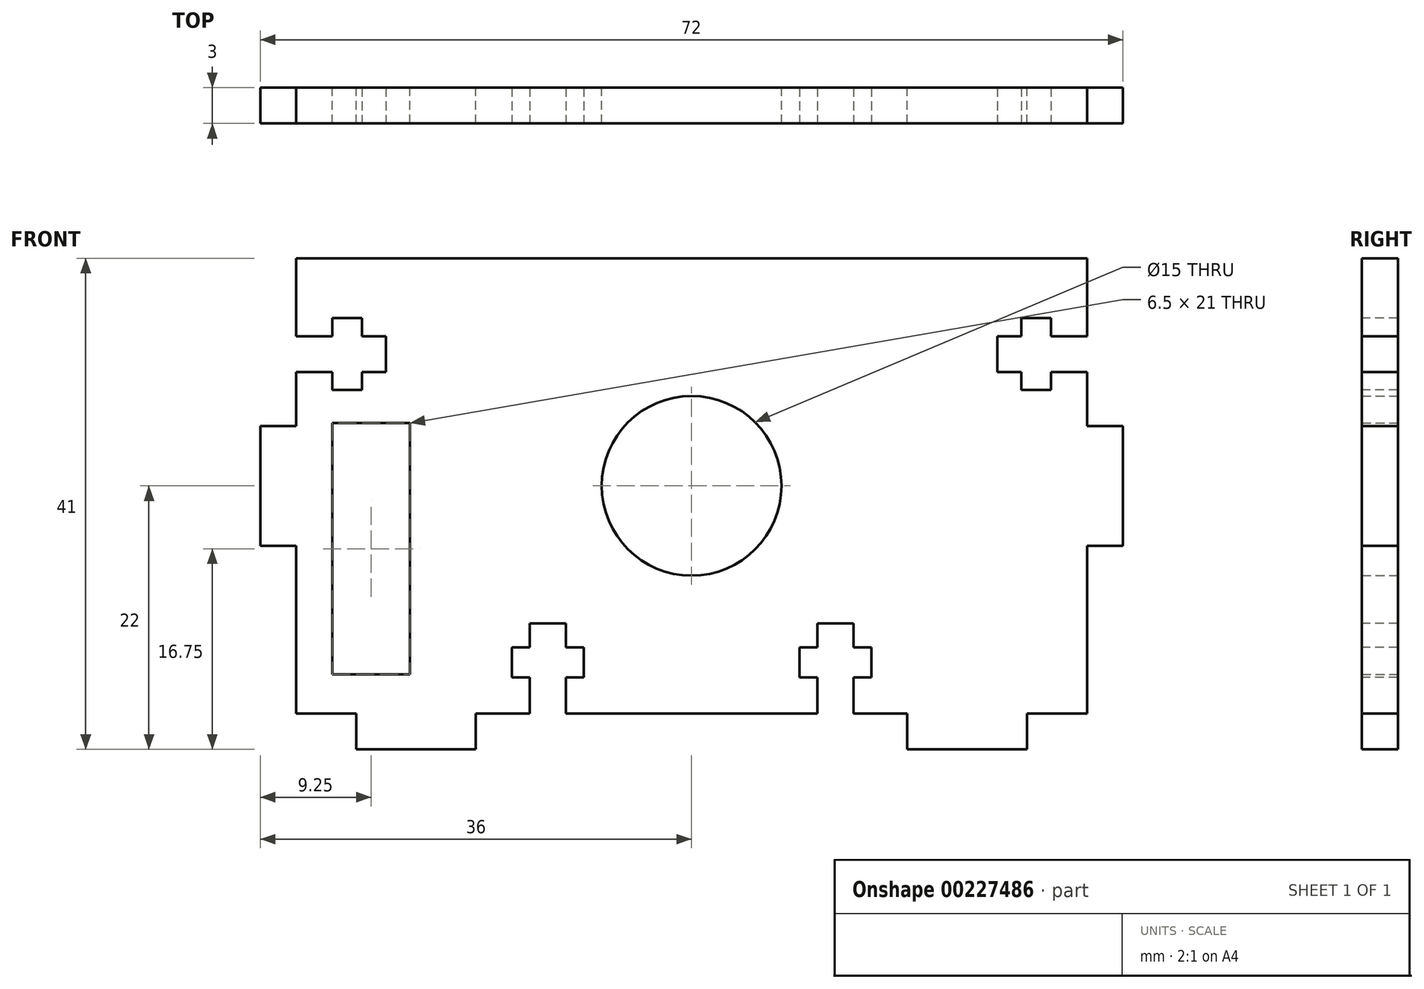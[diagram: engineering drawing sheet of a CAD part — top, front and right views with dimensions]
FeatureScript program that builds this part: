
annotation { "Feature Type Name" : "Feature", "Feature Type Description" : "" }
export const myFeature = defineFeature(function(context is Context, id is Id, definition is map)
    precondition{}
    {
        {
            assignVariable(context, id + "F0", {"name" : "Thickness", "anyValue" : 3});
        }
        {
            var Q0;
            Q0=qCreatedBy(makeId("Front.planeOp"),FACE);
            var sketch = newSketch(context, id + "F1", { "sketchPlane" : qUnion([Q0])});
            skLineSegment(sketch, "E0.top", {"start": v(33, 19) * mm, "end": v(-33, 19) * mm});
            skPoint(sketch, "E0.middle", {"position": v(0, 0) * mm});
            skCircle(sketch, "E1", {"center": v(0, 0) * mm, "radius": 7.5 * mm});
            skPoint(sketch, "E2", {"position": v(0, 19) * mm});
            skLineSegment(sketch, "E3", {"start": v(-28, -19) * mm, "end": v(-28, -22) * mm});
            skLineSegment(sketch, "E4", {"start": v(-28, -22) * mm, "end": v(-18, -22) * mm});
            skLineSegment(sketch, "E5", {"start": v(-18, -22) * mm, "end": v(-18, -19) * mm});
            skLineSegment(sketch, "E6", {"start": v(-18, -19) * mm, "end": v(0, -19) * mm});
            skLineSegment(sketch, "E7.MirrorCS", {"start": v(18, -19) * mm, "end": v(0, -19) * mm});
            skLineSegment(sketch, "E8.MirrorCS", {"start": v(18, -22) * mm, "end": v(18, -19) * mm});
            skLineSegment(sketch, "E9.MirrorCS", {"start": v(28, -22) * mm, "end": v(18, -22) * mm});
            skLineSegment(sketch, "E10.MirrorCS", {"start": v(28, -19) * mm, "end": v(28, -22) * mm});
            skLineSegment(sketch, "E11", {"start": v(-33, -19) * mm, "end": v(-33, -5) * mm});
            skLineSegment(sketch, "E12", {"start": v(-33, -5) * mm, "end": v(-36, -5) * mm});
            skLineSegment(sketch, "E13", {"start": v(-36, -5) * mm, "end": v(-36, 5) * mm});
            skLineSegment(sketch, "E14", {"start": v(-36, 5) * mm, "end": v(-33, 5) * mm});
            skLineSegment(sketch, "E15", {"start": v(-33, 5) * mm, "end": v(-33, 19) * mm});
            skPoint(sketch, "E16", {"position": v(-36, 0) * mm});
            skLineSegment(sketch, "E17.MirrorCS", {"start": v(33, 5) * mm, "end": v(33, 19) * mm});
            skLineSegment(sketch, "E18.MirrorCS", {"start": v(36, 5) * mm, "end": v(33, 5) * mm});
            skLineSegment(sketch, "E19.MirrorCS", {"start": v(36, -5) * mm, "end": v(36, 5) * mm});
            skLineSegment(sketch, "E20.MirrorCS", {"start": v(33, -5) * mm, "end": v(36, -5) * mm});
            skLineSegment(sketch, "E21.MirrorCS", {"start": v(33, -19) * mm, "end": v(33, -5) * mm});
            skLineSegment(sketch, "E22", {"start": v(28, -19) * mm, "end": v(33, -19) * mm});
            skLineSegment(sketch, "E23", {"start": v(-28, -19) * mm, "end": v(-33, -19) * mm});
            skLineSegment(sketch, "E24.bottom", {"start": v(-30, 5.25) * mm, "end": v(-23.5, 5.25) * mm});
            skLineSegment(sketch, "E24.top", {"start": v(-30, -15.75) * mm, "end": v(-23.5, -15.75) * mm});
            skLineSegment(sketch, "E24.left", {"start": v(-30, 5.25) * mm, "end": v(-30, -15.75) * mm});
            skLineSegment(sketch, "E24.right", {"start": v(-23.5, 5.25) * mm, "end": v(-23.5, -15.75) * mm});
            skSolve(sketch);
        }
        {
            var Q0;
            Q0=makeQuery(id+"F1.imprint","IMPRINT",FACE,{"disambiguationData":[TD([[makeQuery(id+"F1.imprint","IMPRINT",EDGE,{"derivedFrom":sQuery(id+"F1.wireOp",EDGE,"E0.bottom")}),-1.0]])]});
            var Q1;
            Q1=makeQuery(id+"F1.imprint","IMPRINT",FACE,{"disambiguationData":[TD([[makeQuery(id+"F1.imprint","IMPRINT",EDGE,{"derivedFrom":sQuery(id+"F1.wireOp",EDGE,"E0.top")}),1.0]])]});
            extrude(context, id + "F2", {"entities" : qUnion([Q0, Q1]), "depth" : (getVariable(context, 'Thickness')) * mm});
        }
        {
            var Q0;
            Q0=makeQuery(id+"F2.opExtrude","CAP_FACE",FACE,{"disambiguationData":[OSD([sQuery(id+"F1.wireOp",EDGE,"E0.top"),sQuery(id+"F1.wireOp",EDGE,"E1"),sQuery(id+"F1.wireOp",EDGE,"i2BJ4We7-Z1tz-6YYD-7Gnh-UwGsJDHukj4o"),sQuery(id+"F1.wireOp",EDGE,"H5TLaSxA-TAvm-WxYI-6s5p-rbUKsHJPtpz8"),sQuery(id+"F1.wireOp",EDGE,"fE5sAuBm-J1N4-LUQK-MxoP-oJGd3h4EWBky"),sQuery(id+"F1.wireOp",EDGE,"UVkaeSOW-HMeC-MlRq-fWxO-58zO0Vm4gzLd"),sQuery(id+"F1.wireOp",EDGE,"4oAcHBtJ-SWL1-Us38-5a5N-tiTYXxMsnVxl"),sQuery(id+"F1.wireOp",EDGE,"MGHFterx-abw6-INuc-nvHV-QaNsLm6ah1ng"),sQuery(id+"F1.wireOp",EDGE,"DztduCwT-NtgE-rZnK-mSEW-EnSqVKOmk10X"),sQuery(id+"F1.wireOp",EDGE,"XImseshz-UxQT-ogDy-5Lvy-O5B2oz8zv5fS"),sQuery(id+"F1.wireOp",EDGE,"FHz1HeJZ-Y50a-yfiC-Rnzm-b0fU7RSFoIpM"),sQuery(id+"F1.wireOp",EDGE,"bBcTDBjg-FDSx-XcTB-SbE1-9syf6QqrHLmC"),sQuery(id+"F1.wireOp",EDGE,"1vXtDNT1-yAZY-NYDk-InIM-wFA5S2rVquaF"),sQuery(id+"F1.wireOp",EDGE,"rcTIoJpC-EadT-N3WT-61kg-b3dVzh2UPf16"),sQuery(id+"F1.wireOp",EDGE,"V9EOst0m-YofT-ZeQ4-KXmd-etc1AHxpQRv2"),sQuery(id+"F1.wireOp",EDGE,"E3"),sQuery(id+"F1.wireOp",EDGE,"E4"),sQuery(id+"F1.wireOp",EDGE,"E5"),sQuery(id+"F1.wireOp",EDGE,"E6"),sQuery(id+"F1.wireOp",EDGE,"E7.MirrorCS"),sQuery(id+"F1.wireOp",EDGE,"E8.MirrorCS"),sQuery(id+"F1.wireOp",EDGE,"E9.MirrorCS"),sQuery(id+"F1.wireOp",EDGE,"E10.MirrorCS"),sQuery(id+"F1.wireOp",EDGE,"4fc586d0-1a2d-4033-9ad1-b4b14924f1e60.MirrorCS"),sQuery(id+"F1.wireOp",EDGE,"25921314-2feb-4960-9358-c6f40c29e8060.MirrorCS"),sQuery(id+"F1.wireOp",EDGE,"92609e8c-4cca-44cb-b192-d1e8ea80d6400.MirrorCS"),sQuery(id+"F1.wireOp",EDGE,"c6435143-3ef5-4a16-a53c-0c7a1f294e250.MirrorCS"),sQuery(id+"F1.wireOp",EDGE,"302a1fd6-7f51-4dcd-b85b-b87c70c5ff6f0.MirrorCS"),sQuery(id+"F1.wireOp",EDGE,"271ff51f-9e70-48b1-9ca4-6ffa4ba6ee090.MirrorCS"),sQuery(id+"F1.wireOp",EDGE,"7c8ad784-0027-4aca-88da-cb9512f49f770.MirrorCS"),sQuery(id+"F1.wireOp",EDGE,"aab8c399-5e78-4643-9a76-05bc1427fb740.MirrorCS"),sQuery(id+"F1.wireOp",EDGE,"2a5f69ab-9c37-4cf4-a27a-83d52b59f34f0.MirrorCS"),sQuery(id+"F1.wireOp",EDGE,"8a72d888-9ff6-4074-9ea7-52382edc54d80.MirrorCS"),sQuery(id+"F1.wireOp",EDGE,"2b144515-558f-4b7e-bfd9-8a7150f656b50.MirrorCS"),sQuery(id+"F1.wireOp",EDGE,"7271def4-b984-4847-8607-e135956054630.MirrorCS"),sQuery(id+"F1.wireOp",EDGE,"d1406031-9f0b-476a-854e-e83de3dd73970.MirrorCS"),sQuery(id+"F1.wireOp",EDGE,"E11"),sQuery(id+"F1.wireOp",EDGE,"E12"),sQuery(id+"F1.wireOp",EDGE,"E13"),sQuery(id+"F1.wireOp",EDGE,"E14"),sQuery(id+"F1.wireOp",EDGE,"E15"),sQuery(id+"F1.wireOp",EDGE,"E17.MirrorCS"),sQuery(id+"F1.wireOp",EDGE,"E18.MirrorCS"),sQuery(id+"F1.wireOp",EDGE,"E19.MirrorCS"),sQuery(id+"F1.wireOp",EDGE,"E20.MirrorCS"),sQuery(id+"F1.wireOp",EDGE,"E21.MirrorCS")])],"isStart":false});
            var sketch = newSketch(context, id + "F3", { "sketchPlane" : qUnion([Q0])});
            skLineSegment(sketch, "E25", {"start": v(10.5, -19) * mm, "end": v(10.5, -16) * mm});
            skLineSegment(sketch, "E26", {"start": v(10.5, -16) * mm, "end": v(9, -16) * mm});
            skLineSegment(sketch, "E27", {"start": v(9, -16) * mm, "end": v(9, -13.5) * mm});
            skLineSegment(sketch, "E28", {"start": v(9, -13.5) * mm, "end": v(10.5, -13.5) * mm});
            skLineSegment(sketch, "E29", {"start": v(10.5, -13.5) * mm, "end": v(10.5, -11.5) * mm});
            skLineSegment(sketch, "E30", {"start": v(10.5, -11.5) * mm, "end": v(13.5, -11.5) * mm});
            skLineSegment(sketch, "E31", {"start": v(13.5, -11.5) * mm, "end": v(13.5, -13.5) * mm});
            skLineSegment(sketch, "E32", {"start": v(13.5, -13.5) * mm, "end": v(15, -13.5) * mm});
            skLineSegment(sketch, "E33", {"start": v(15, -13.5) * mm, "end": v(15, -16) * mm});
            skLineSegment(sketch, "E34", {"start": v(15, -16) * mm, "end": v(13.5, -16) * mm});
            skLineSegment(sketch, "E35", {"start": v(13.5, -16) * mm, "end": v(13.5, -19) * mm});
            skPoint(sketch, "E36", {"position": v(12, -19) * mm});
            skLineSegment(sketch, "E37", {"start": v(13.5, -19) * mm, "end": v(10.5, -19) * mm});
            skLineSegment(sketch, "E38", {"start": v(30, 9.5) * mm, "end": v(30, 8) * mm});
            skLineSegment(sketch, "E39", {"start": v(30, 8) * mm, "end": v(27.5, 8) * mm});
            skLineSegment(sketch, "E40", {"start": v(27.5, 8) * mm, "end": v(27.5, 9.5) * mm});
            skLineSegment(sketch, "E41", {"start": v(27.5, 9.5) * mm, "end": v(25.5, 9.5) * mm});
            skLineSegment(sketch, "E42", {"start": v(25.5, 9.5) * mm, "end": v(25.5, 12.5) * mm});
            skLineSegment(sketch, "E43", {"start": v(25.5, 12.5) * mm, "end": v(27.5, 12.5) * mm});
            skLineSegment(sketch, "E44", {"start": v(27.5, 12.5) * mm, "end": v(27.5, 14) * mm});
            skLineSegment(sketch, "E45", {"start": v(27.5, 14) * mm, "end": v(30, 14) * mm});
            skLineSegment(sketch, "E46", {"start": v(30, 14) * mm, "end": v(30, 12.5) * mm});
            skLineSegment(sketch, "E47", {"start": v(30, 12.5) * mm, "end": v(33, 12.5) * mm});
            skLineSegment(sketch, "E48.MirrorCS", {"start": v(-10.5, -16) * mm, "end": v(-9, -16) * mm});
            skLineSegment(sketch, "E49.MirrorCS", {"start": v(-9, -13.5) * mm, "end": v(-10.5, -13.5) * mm});
            skLineSegment(sketch, "E50.MirrorCS", {"start": v(-15, -16) * mm, "end": v(-13.5, -16) * mm});
            skLineSegment(sketch, "E51.MirrorCS", {"start": v(-13.5, -13.5) * mm, "end": v(-15, -13.5) * mm});
            skLineSegment(sketch, "E52.MirrorCS", {"start": v(-10.5, -13.5) * mm, "end": v(-10.5, -11.5) * mm});
            skLineSegment(sketch, "E53.MirrorCS", {"start": v(-13.5, -19) * mm, "end": v(-10.5, -19) * mm});
            skLineSegment(sketch, "E54.MirrorCS", {"start": v(-9, -16) * mm, "end": v(-9, -13.5) * mm});
            skPoint(sketch, "E55.MirrorP", {"position": v(-12, -19) * mm});
            skLineSegment(sketch, "E56.MirrorCS", {"start": v(-10.5, -19) * mm, "end": v(-10.5, -16) * mm});
            skLineSegment(sketch, "E57.MirrorCS", {"start": v(-10.5, -11.5) * mm, "end": v(-13.5, -11.5) * mm});
            skLineSegment(sketch, "E58.MirrorCS", {"start": v(-13.5, -11.5) * mm, "end": v(-13.5, -13.5) * mm});
            skLineSegment(sketch, "E59.MirrorCS", {"start": v(-13.5, -16) * mm, "end": v(-13.5, -19) * mm});
            skLineSegment(sketch, "E60.MirrorCS", {"start": v(-15, -13.5) * mm, "end": v(-15, -16) * mm});
            skLineSegment(sketch, "E61", {"start": v(30, 9.5) * mm, "end": v(33, 9.5) * mm});
            skLineSegment(sketch, "E62", {"start": v(33, 9.5) * mm, "end": v(33, 12.5) * mm});
            skPoint(sketch, "E63", {"position": v(33, 11) * mm});
            skLineSegment(sketch, "E64.MirrorCS", {"start": v(-25.5, 12.5) * mm, "end": v(-27.5, 12.5) * mm});
            skLineSegment(sketch, "E65.MirrorCS", {"start": v(-27.5, 9.5) * mm, "end": v(-25.5, 9.5) * mm});
            skLineSegment(sketch, "E66.MirrorCS", {"start": v(-25.5, 9.5) * mm, "end": v(-25.5, 12.5) * mm});
            skLineSegment(sketch, "E67.MirrorCS", {"start": v(-30, 14) * mm, "end": v(-30, 12.5) * mm});
            skLineSegment(sketch, "E68.MirrorCS", {"start": v(-30, 12.5) * mm, "end": v(-33, 12.5) * mm});
            skLineSegment(sketch, "E69.MirrorCS", {"start": v(-30, 9.5) * mm, "end": v(-30, 8) * mm});
            skLineSegment(sketch, "E70.MirrorCS", {"start": v(-30, 9.5) * mm, "end": v(-33, 9.5) * mm});
            skLineSegment(sketch, "E71.MirrorCS", {"start": v(-27.5, 12.5) * mm, "end": v(-27.5, 14) * mm});
            skLineSegment(sketch, "E72.MirrorCS", {"start": v(-27.5, 8) * mm, "end": v(-27.5, 9.5) * mm});
            skLineSegment(sketch, "E73.MirrorCS", {"start": v(-30, 8) * mm, "end": v(-27.5, 8) * mm});
            skLineSegment(sketch, "E74.MirrorCS", {"start": v(-27.5, 14) * mm, "end": v(-30, 14) * mm});
            skLineSegment(sketch, "E75.MirrorCS", {"start": v(-33, 9.5) * mm, "end": v(-33, 12.5) * mm});
            skPoint(sketch, "E76.MirrorP", {"position": v(-33, 11) * mm});
            skSolve(sketch);
        }
        {
            var Q0;
            Q0=makeQuery(id+"F3.imprint","IMPRINT",FACE,{"disambiguationData":[TD([[makeQuery(id+"F3.imprint","IMPRINT",EDGE,{"derivedFrom":sQuery(id+"F3.wireOp",EDGE,"edad8c0f-5398-4aec-a5a4-76bc5562e620")}),-1.0]])]});
            var Q1;
            Q1=makeQuery(id+"F3.imprint","IMPRINT",FACE,{"disambiguationData":[TD([[makeQuery(id+"F3.imprint","IMPRINT",EDGE,{"derivedFrom":sQuery(id+"F3.wireOp",EDGE,"E25")}),-1.0]])]});
            var Q2;
            Q2=makeQuery(id+"F3.imprint","IMPRINT",FACE,{"disambiguationData":[TD([[makeQuery(id+"F3.imprint","IMPRINT",EDGE,{"derivedFrom":sQuery(id+"F3.wireOp",EDGE,"E48.MirrorCS")}),1.0]])]});
            var Q3;
            Q3=makeQuery(id+"F3.imprint","IMPRINT",FACE,{"disambiguationData":[TD([[makeQuery(id+"F3.imprint","IMPRINT",EDGE,{"derivedFrom":sQuery(id+"F3.wireOp",EDGE,"7cc48e27-ac2b-45f1-a2cc-41954da226e80.MirrorCS")}),1.0]])]});
            var Q4;
            Q4=makeQuery(id+"F3.imprint","IMPRINT",FACE,{"disambiguationData":[TD([[makeQuery(id+"F3.imprint","IMPRINT",EDGE,{"derivedFrom":sQuery(id+"F3.wireOp",EDGE,"E38")}),-1.0]])]});
            var Q5;
            Q5=makeQuery(id+"F3.imprint","IMPRINT",FACE,{"disambiguationData":[TD([[makeQuery(id+"F3.imprint","IMPRINT",EDGE,{"derivedFrom":sQuery(id+"F3.wireOp",EDGE,"E64.MirrorCS")}),1.0]])]});
            extrude(context, id + "F4", {"entities" : qUnion([Q0, Q1, Q2, Q3, Q4, Q5]), "operationType" : NewBodyOperationType.REMOVE, "endBound" : BoundingType.UP_TO_NEXT, "oppositeDirection" : true, "depth" : 25 * mm});
        }
    });
